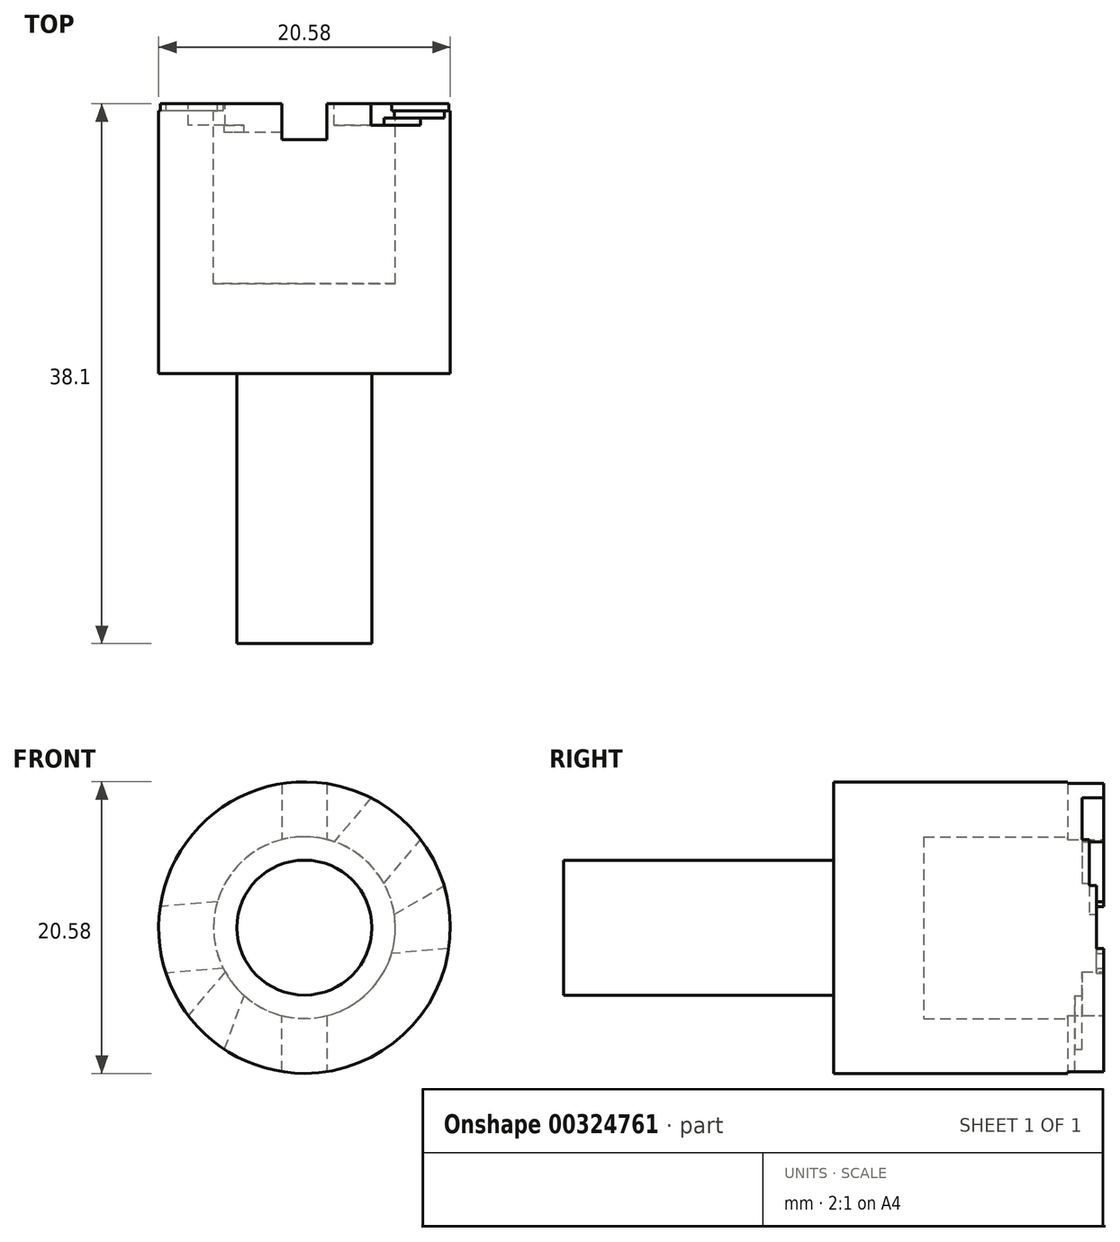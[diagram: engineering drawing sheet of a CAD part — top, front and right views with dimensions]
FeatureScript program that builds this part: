
annotation { "Feature Type Name" : "Feature", "Feature Type Description" : "" }
export const myFeature = defineFeature(function(context is Context, id is Id, definition is map)
    precondition{}
    {
        {
            var Q0;
            Q0=qCreatedBy(makeId("Front.planeOp"),FACE);
            var sketch = newSketch(context, id + "F0", { "sketchPlane" : qUnion([Q0])});
            skCircle(sketch, "E0", {"center": v(0, 0) * mm, "radius": 10.29 * mm});
            skSolve(sketch);
        }
        {
            var Q0;
            Q0=makeQuery(id+"F0.imprint","IMPRINT",FACE,{"disambiguationData":[TD([[makeQuery(id+"F0.imprint","IMPRINT",EDGE,{"derivedFrom":sQuery(id+"F0.wireOp",EDGE,"E0")}),1.0]])]});
            extrude(context, id + "F1", {"entities" : qUnion([Q0]), "depth" : 38.1 * mm, "offsetDistance" : 25.4 * mm});
        }
        {
            var Q0;
            Q0=makeQuery(id+"F1.opExtrude","CAP_FACE",FACE,{"disambiguationData":[OSD([sQuery(id+"F0.wireOp",EDGE,"E0")])],"isStart":false});
            var sketch = newSketch(context, id + "F2", { "sketchPlane" : qUnion([Q0])});
            skCircle(sketch, "E1", {"center": v(0, 0) * mm, "radius": 4.76 * mm});
            skCircle(sketch, "E2", {"center": v(0, 0) * mm, "radius": 10.29 * mm});
            skSolve(sketch);
        }
        {
            var Q0;
            Q0=makeQuery(id+"F2.imprint","IMPRINT",FACE,{"disambiguationData":[TD([[makeQuery(id+"F2.imprint","IMPRINT",EDGE,{"derivedFrom":sQuery(id+"F2.wireOp",EDGE,"E1")}),-1.0]])]});
            extrude(context, id + "F3", {"entities" : qUnion([Q0]), "operationType" : NewBodyOperationType.REMOVE, "oppositeDirection" : true, "depth" : 19.05 * mm, "offsetDistance" : 25.4 * mm});
        }
        {
            var Q0;
            Q0=makeQuery(id+"F1.opExtrude","CAP_FACE",FACE,{"disambiguationData":[OSD([sQuery(id+"F0.wireOp",EDGE,"E0")])],"isStart":true});
            var sketch = newSketch(context, id + "F4", { "sketchPlane" : qUnion([Q0])});
            skCircle(sketch, "E3", {"center": v(0, 0) * mm, "radius": 6.41 * mm});
            skSolve(sketch);
        }
        {
            var Q0;
            Q0=makeQuery(id+"F4.imprint","IMPRINT",FACE,{"disambiguationData":[TD([[makeQuery(id+"F4.imprint","IMPRINT",EDGE,{"derivedFrom":sQuery(id+"F4.wireOp",EDGE,"E3")}),1.0]])]});
            extrude(context, id + "F5", {"entities" : qUnion([Q0]), "operationType" : NewBodyOperationType.REMOVE, "oppositeDirection" : true, "depth" : 12.7 * mm, "offsetDistance" : 25.4 * mm});
        }
        {
            var Q0;
            Q0=makeQuery(id+"F1.opExtrude","CAP_FACE",FACE,{"disambiguationData":[OSD([sQuery(id+"F0.wireOp",EDGE,"E0")])],"isStart":true});
            var sketch = newSketch(context, id + "F6", { "sketchPlane" : qUnion([Q0])});
            skLineSegment(sketch, "E4.bottom", {"start": v(-1.57, 12.92) * mm, "end": v(1.6, 12.92) * mm});
            skLineSegment(sketch, "E4.top", {"start": v(-1.57, -12.85) * mm, "end": v(1.6, -12.85) * mm});
            skLineSegment(sketch, "E4.left", {"start": v(-1.57, 12.92) * mm, "end": v(-1.57, -12.85) * mm});
            skLineSegment(sketch, "E4.right", {"start": v(1.6, 12.92) * mm, "end": v(1.6, -12.85) * mm});
            skSolve(sketch);
        }
        {
            var Q0;
            {var subQ0=sQuery(id+"F6.wireOp",EDGE,"E4.left");var subQ1=makeQuery(id+"F1.opExtrude","CAP_EDGE",EDGE,{"disambiguationData":[OSD([sQuery(id+"F0.wireOp",EDGE,"E0")])],"isStart":true});var subQ2=makeQuery(id+"F6.imprint","INTERSECT",VERTEX,{"disambiguationData":[OD(0.0)],"derivedFrom":[subQ1,subQ0]});Q0=makeQuery(id+"F6.imprint","IMPRINT",FACE,{"disambiguationData":[TD([[makeQuery(id+"F6.imprint","IMPRINT",EDGE,{"disambiguationData":[TD([[subQ2,-1.0]])],"derivedFrom":subQ0}),1.0]])]});}
            var Q1;
            {var subQ0=sQuery(id+"F6.wireOp",EDGE,"E4.left");var subQ1=makeQuery(id+"F1.opExtrude","CAP_EDGE",EDGE,{"disambiguationData":[OSD([sQuery(id+"F0.wireOp",EDGE,"E0")])],"isStart":true});var subQ2=makeQuery(id+"F6.imprint","INTERSECT",VERTEX,{"disambiguationData":[OD(1.0)],"derivedFrom":[subQ1,subQ0]});Q1=makeQuery(id+"F6.imprint","IMPRINT",FACE,{"disambiguationData":[TD([[makeQuery(id+"F6.imprint","IMPRINT",EDGE,{"disambiguationData":[TD([[subQ2,1.0]])],"derivedFrom":subQ0}),1.0]])]});}
            extrude(context, id + "F7", {"entities" : qUnion([Q0, Q1]), "operationType" : NewBodyOperationType.REMOVE, "oppositeDirection" : true, "depth" : 2.54 * mm, "offsetDistance" : 25.4 * mm});
        }
        {
            var Q0;
            {var subQ0=sQuery(id+"F0.wireOp",EDGE,"E0");var subQ2=sQuery(id+"F6.wireOp",EDGE,"E4.left");var subQ3=makeQuery(id+"F1.opExtrude","CAP_EDGE",EDGE,{"disambiguationData":[OSD([subQ0])],"isStart":true});Q0=makeQuery(id+"F7.boolean.opBoolean","SPLIT",FACE,{"disambiguationData":[TD([makeQuery(id+"F7.opExtrude","SWEPT_FACE",FACE,{"disambiguationData":[OSD([subQ2]),TDD([makeQuery(id+"F6.imprint","IMPRINT",EDGE,{"disambiguationData":[TD([[makeQuery(id+"F6.imprint","INTERSECT",VERTEX,{"disambiguationData":[OD(0.0)],"derivedFrom":[subQ3,subQ2]}),-1.0]])],"derivedFrom":subQ2})])]})])],"derivedFrom":makeQuery(id+"F1.opExtrude","CAP_FACE",FACE,{"disambiguationData":[OSD([subQ0])],"isStart":true})});}
            var sketch = newSketch(context, id + "F8", { "sketchPlane" : qUnion([Q0])});
            skLineSegment(sketch, "E5", {"start": v(0, 0) * mm, "end": v(-4.44, 12.2) * mm, "construction": true});
            skLineSegment(sketch, "E6", {"start": v(-6.13, 9.93) * mm, "end": v(1.69, -11.55) * mm});
            skLineSegment(sketch, "E7.MirrorCS", {"start": v(-1.69, 11.55) * mm, "end": v(6.13, -9.93) * mm});
            skLineSegment(sketch, "E8", {"start": v(-6.13, 9.93) * mm, "end": v(-1.69, 11.55) * mm});
            skLineSegment(sketch, "E9", {"start": v(1.69, -11.55) * mm, "end": v(6.13, -9.93) * mm});
            skSolve(sketch);
        }
        {
            var Q0;
            {var subQ1=sQuery(id+"F0.wireOp",EDGE,"E0");var subQ3=sQuery(id+"F6.wireOp",EDGE,"E4.left");var subQ4=makeQuery(id+"F1.opExtrude","CAP_EDGE",EDGE,{"disambiguationData":[OSD([subQ1])],"isStart":true});var subQ7=makeQuery(id+"F6.imprint","IMPRINT",EDGE,{"disambiguationData":[TD([[makeQuery(id+"F6.imprint","INTERSECT",VERTEX,{"disambiguationData":[OD(0.0)],"derivedFrom":[subQ4,subQ3]}),-1.0]])],"derivedFrom":subQ3});var subQ14=makeQuery(id+"F7.boolean.opBoolean","COPY",EDGE,{"derivedFrom":makeQuery(id+"F7.opExtrude","CAP_EDGE",EDGE,{"disambiguationData":[OSD([subQ3]),TDD([subQ7])],"isStart":true})});Q0=makeQuery(id+"F8.imprint","IMPRINT",FACE,{"disambiguationData":[TD([[makeQuery(id+"F8.imprint","IMPRINT",EDGE,{"derivedFrom":subQ14}),-1.0]])]});}
            var Q1;
            Q1=makeQuery(id+"F8.imprint","IMPRINT",FACE,{"disambiguationData":[TD([[makeQuery(id+"F8.imprint","IMPRINT",EDGE,{"derivedFrom":sQuery(id+"F8.wireOp",EDGE,"E7.MirrorCS")}),-1.0]])]});
            var Q2;
            {var subQ1=sQuery(id+"F0.wireOp",EDGE,"E0");var subQ3=sQuery(id+"F6.wireOp",EDGE,"E4.left");var subQ4=makeQuery(id+"F1.opExtrude","CAP_EDGE",EDGE,{"disambiguationData":[OSD([subQ1])],"isStart":true});var subQ7=makeQuery(id+"F6.imprint","IMPRINT",EDGE,{"disambiguationData":[TD([[makeQuery(id+"F6.imprint","INTERSECT",VERTEX,{"disambiguationData":[OD(0.0)],"derivedFrom":[subQ4,subQ3]}),-1.0]])],"derivedFrom":subQ3});var subQ12=sQuery(id+"F8.wireOp",EDGE,"E7.MirrorCS");var subQ15=makeQuery(id+"F7.boolean.opBoolean","COPY",EDGE,{"derivedFrom":makeQuery(id+"F7.opExtrude","CAP_EDGE",EDGE,{"disambiguationData":[OSD([subQ3]),TDD([subQ7])],"isStart":true})});var subQ17=makeQuery(id+"F8.imprint","INTERSECT",VERTEX,{"derivedFrom":[subQ15,subQ12]});Q2=makeQuery(id+"F8.imprint","IMPRINT",FACE,{"disambiguationData":[TD([[makeQuery(id+"F8.imprint","IMPRINT",EDGE,{"disambiguationData":[TD([[subQ17,1.0]])],"derivedFrom":subQ12}),-1.0]])]});}
            var Q3;
            {var subQ11=sQuery(id+"F8.wireOp",EDGE,"E9");Q3=makeQuery(id+"F8.imprint","IMPRINT",FACE,{"disambiguationData":[TD([[makeQuery(id+"F8.imprint","IMPRINT",EDGE,{"derivedFrom":subQ11}),1.0]])]});}
            extrude(context, id + "F9", {"entities" : qUnion([Q0, Q1, Q2, Q3]), "operationType" : NewBodyOperationType.REMOVE, "oppositeDirection" : true, "depth" : 2.03 * mm, "offsetDistance" : 25.4 * mm});
        }
        {
            var Q0;
            {var subQ0=sQuery(id+"F0.wireOp",EDGE,"E0");var subQ2=sQuery(id+"F6.wireOp",EDGE,"E4.left");var subQ3=makeQuery(id+"F1.opExtrude","CAP_EDGE",EDGE,{"disambiguationData":[OSD([subQ0])],"isStart":true});Q0=makeQuery(id+"F7.boolean.opBoolean","SPLIT",FACE,{"disambiguationData":[TD([makeQuery(id+"F7.opExtrude","SWEPT_FACE",FACE,{"disambiguationData":[OSD([subQ2]),TDD([makeQuery(id+"F6.imprint","IMPRINT",EDGE,{"disambiguationData":[TD([[makeQuery(id+"F6.imprint","INTERSECT",VERTEX,{"disambiguationData":[OD(0.0)],"derivedFrom":[subQ3,subQ2]}),-1.0]])],"derivedFrom":subQ2})])]})])],"derivedFrom":makeQuery(id+"F1.opExtrude","CAP_FACE",FACE,{"disambiguationData":[OSD([subQ0])],"isStart":true})});}
            var sketch = newSketch(context, id + "F10", { "sketchPlane" : qUnion([Q0])});
            skLineSegment(sketch, "E10", {"start": v(0, 0) * mm, "end": v(-6.57, 7.83) * mm, "construction": true});
            skLineSegment(sketch, "E11", {"start": v(-9.1, 7.29) * mm, "end": v(5.6, -10.23) * mm});
            skLineSegment(sketch, "E12.MirrorCS", {"start": v(-5.6, 10.23) * mm, "end": v(9.1, -7.29) * mm});
            skLineSegment(sketch, "E13", {"start": v(-5.6, 10.23) * mm, "end": v(-9.1, 7.29) * mm});
            skLineSegment(sketch, "E14", {"start": v(5.6, -10.23) * mm, "end": v(9.1, -7.29) * mm});
            skSolve(sketch);
        }
        {
            var Q0;
            {var subQ13=makeQuery(id+"F9.boolean.opBoolean","COPY",EDGE,{"derivedFrom":makeQuery(id+"F9.opExtrude","CAP_EDGE",EDGE,{"disambiguationData":[OSD([sQuery(id+"F8.wireOp",EDGE,"E6")])],"isStart":true})});Q0=makeQuery(id+"F10.imprint","IMPRINT",FACE,{"disambiguationData":[TD([[makeQuery(id+"F10.imprint","IMPRINT",EDGE,{"derivedFrom":subQ13}),-1.0]])]});}
            var Q1;
            Q1=makeQuery(id+"F10.imprint","IMPRINT",FACE,{"disambiguationData":[TD([[makeQuery(id+"F10.imprint","IMPRINT",EDGE,{"derivedFrom":sQuery(id+"F10.wireOp",EDGE,"E12.MirrorCS")}),-1.0]])]});
            var Q2;
            {var subQ2=sQuery(id+"F8.wireOp",EDGE,"E6");var subQ4=sQuery(id+"F4.wireOp",EDGE,"E3");var subQ5=makeQuery(id+"F5.boolean.opBoolean","COPY",FACE,{"derivedFrom":makeQuery(id+"F5.opExtrude","SWEPT_FACE",FACE,{"disambiguationData":[OSD([subQ4])]})});var subQ6=makeQuery(id+"F9.boolean.opBoolean","COPY",EDGE,{"disambiguationData":[TD([subQ5])],"derivedFrom":makeQuery(id+"F9.opExtrude","CAP_EDGE",EDGE,{"disambiguationData":[OSD([subQ2])],"isStart":true})});var subQ16=sQuery(id+"F10.wireOp",EDGE,"E12.MirrorCS");var subQ19=makeQuery(id+"F10.imprint","INTERSECT",VERTEX,{"derivedFrom":[subQ6,subQ16]});Q2=makeQuery(id+"F10.imprint","IMPRINT",FACE,{"disambiguationData":[TD([[makeQuery(id+"F10.imprint","IMPRINT",EDGE,{"disambiguationData":[TD([[subQ19,1.0]])],"derivedFrom":subQ16}),-1.0]])]});}
            var Q3;
            {var subQ13=sQuery(id+"F10.wireOp",EDGE,"E14");Q3=makeQuery(id+"F10.imprint","IMPRINT",FACE,{"disambiguationData":[TD([[makeQuery(id+"F10.imprint","IMPRINT",EDGE,{"derivedFrom":subQ13}),1.0]])]});}
            extrude(context, id + "F11", {"entities" : qUnion([Q0, Q1, Q2, Q3]), "operationType" : NewBodyOperationType.REMOVE, "oppositeDirection" : true, "depth" : 1.52 * mm, "offsetDistance" : 25.4 * mm});
        }
        {
            var Q0;
            {var subQ0=sQuery(id+"F0.wireOp",EDGE,"E0");var subQ2=sQuery(id+"F6.wireOp",EDGE,"E4.right");var subQ3=makeQuery(id+"F1.opExtrude","CAP_EDGE",EDGE,{"disambiguationData":[OSD([subQ0])],"isStart":true});Q0=makeQuery(id+"F7.boolean.opBoolean","SPLIT",FACE,{"disambiguationData":[TD([makeQuery(id+"F7.opExtrude","SWEPT_FACE",FACE,{"disambiguationData":[OSD([subQ2]),TDD([makeQuery(id+"F6.imprint","IMPRINT",EDGE,{"disambiguationData":[TD([[makeQuery(id+"F6.imprint","INTERSECT",VERTEX,{"disambiguationData":[OD(0.0)],"derivedFrom":[subQ3,subQ2]}),-1.0]])],"derivedFrom":subQ2})])]})])],"derivedFrom":makeQuery(id+"F1.opExtrude","CAP_FACE",FACE,{"disambiguationData":[OSD([subQ0])],"isStart":true})});}
            var sketch = newSketch(context, id + "F12", { "sketchPlane" : qUnion([Q0])});
            skLineSegment(sketch, "E15", {"start": v(0, 0) * mm, "end": v(-19.87, 11.47) * mm, "construction": true});
            skLineSegment(sketch, "E16", {"start": v(-17.08, 7.13) * mm, "end": v(15.38, -11.6) * mm});
            skLineSegment(sketch, "E17.MirrorCS", {"start": v(-14.71, 11.22) * mm, "end": v(17.74, -7.52) * mm});
            skLineSegment(sketch, "E18", {"start": v(-17.08, 7.13) * mm, "end": v(-14.71, 11.22) * mm});
            skLineSegment(sketch, "E19", {"start": v(17.74, -7.52) * mm, "end": v(15.38, -11.6) * mm});
            skSolve(sketch);
        }
        {
            var Q0;
            Q0=makeQuery(id+"F12.imprint","IMPRINT",FACE,{"disambiguationData":[TD([[makeQuery(id+"F12.imprint","IMPRINT",EDGE,{"derivedFrom":sQuery(id+"F12.wireOp",EDGE,"E16")}),1.0]])]});
            var Q1;
            {var subQ13=makeQuery(id+"F11.boolean.opBoolean","COPY",EDGE,{"derivedFrom":makeQuery(id+"F11.opExtrude","CAP_EDGE",EDGE,{"disambiguationData":[OSD([sQuery(id+"F10.wireOp",EDGE,"E12.MirrorCS")])],"isStart":true})});Q1=makeQuery(id+"F12.imprint","IMPRINT",FACE,{"disambiguationData":[TD([[makeQuery(id+"F12.imprint","IMPRINT",EDGE,{"derivedFrom":subQ13}),1.0]])]});}
            var Q2;
            {var subQ14=sQuery(id+"F12.wireOp",EDGE,"E18");Q2=makeQuery(id+"F12.imprint","IMPRINT",FACE,{"disambiguationData":[TD([[makeQuery(id+"F12.imprint","IMPRINT",EDGE,{"derivedFrom":subQ14}),-1.0]])]});}
            var Q3;
            {var subQ10=sQuery(id+"F10.wireOp",EDGE,"E12.MirrorCS");var subQ13=makeQuery(id+"F10.imprint","IMPRINT",EDGE,{"disambiguationData":[TD([[makeQuery(id+"F10.imprint","INTERSECT",VERTEX,{"derivedFrom":[subQ10,sQuery(id+"F10.wireOp",EDGE,"E14")]}),1.0]])],"derivedFrom":subQ10});var subQ14=makeQuery(id+"F11.boolean.opBoolean","COPY",EDGE,{"derivedFrom":makeQuery(id+"F11.opExtrude","CAP_EDGE",EDGE,{"disambiguationData":[OSD([subQ10]),TDD([subQ13])],"isStart":true})});var subQ23=sQuery(id+"F12.wireOp",EDGE,"E16");var subQ24=makeQuery(id+"F12.imprint","INTERSECT",VERTEX,{"derivedFrom":[subQ14,subQ23]});Q3=makeQuery(id+"F12.imprint","IMPRINT",FACE,{"disambiguationData":[TD([[makeQuery(id+"F12.imprint","IMPRINT",EDGE,{"disambiguationData":[TD([[subQ24,1.0]])],"derivedFrom":subQ14}),1.0]])]});}
            extrude(context, id + "F13", {"entities" : qUnion([Q0, Q1, Q2, Q3]), "operationType" : NewBodyOperationType.REMOVE, "oppositeDirection" : true, "depth" : 1.02 * mm, "offsetDistance" : 25.4 * mm});
        }
        {
            var Q0;
            {var subQ0=sQuery(id+"F0.wireOp",EDGE,"E0");var subQ2=sQuery(id+"F6.wireOp",EDGE,"E4.left");var subQ3=makeQuery(id+"F1.opExtrude","CAP_EDGE",EDGE,{"disambiguationData":[OSD([subQ0])],"isStart":true});Q0=makeQuery(id+"F7.boolean.opBoolean","SPLIT",FACE,{"disambiguationData":[TD([makeQuery(id+"F7.opExtrude","SWEPT_FACE",FACE,{"disambiguationData":[OSD([subQ2]),TDD([makeQuery(id+"F6.imprint","IMPRINT",EDGE,{"disambiguationData":[TD([[makeQuery(id+"F6.imprint","INTERSECT",VERTEX,{"disambiguationData":[OD(0.0)],"derivedFrom":[subQ3,subQ2]}),-1.0]])],"derivedFrom":subQ2})])]})])],"derivedFrom":makeQuery(id+"F1.opExtrude","CAP_FACE",FACE,{"disambiguationData":[OSD([subQ0])],"isStart":true})});}
            var sketch = newSketch(context, id + "F14", { "sketchPlane" : qUnion([Q0])});
            skLineSegment(sketch, "E20", {"start": v(0, 0) * mm, "end": v(-33.9, 2.97) * mm, "construction": true});
            skLineSegment(sketch, "E21", {"start": v(-26.22, -0.08) * mm, "end": v(22.55, -4.34) * mm});
            skLineSegment(sketch, "E22.MirrorCS", {"start": v(-25.8, 4.63) * mm, "end": v(22.96, 0.36) * mm});
            skLineSegment(sketch, "E23", {"start": v(-26.22, -0.08) * mm, "end": v(-25.8, 4.63) * mm});
            skLineSegment(sketch, "E24", {"start": v(22.96, 0.36) * mm, "end": v(22.55, -4.34) * mm});
            skSolve(sketch);
        }
        {
            var Q0;
            {var subQ15=sQuery(id+"F14.wireOp",EDGE,"E24");Q0=makeQuery(id+"F14.imprint","IMPRINT",FACE,{"disambiguationData":[TD([[makeQuery(id+"F14.imprint","IMPRINT",EDGE,{"derivedFrom":subQ15}),-1.0]])]});}
            var Q1;
            {var subQ10=sQuery(id+"F12.wireOp",EDGE,"E16");var subQ14=makeQuery(id+"F12.imprint","IMPRINT",EDGE,{"disambiguationData":[TD([[makeQuery(id+"F12.imprint","INTERSECT",VERTEX,{"derivedFrom":[subQ10,sQuery(id+"F12.wireOp",EDGE,"E18")]}),-1.0]])],"derivedFrom":subQ10});var subQ15=makeQuery(id+"F13.boolean.opBoolean","COPY",EDGE,{"derivedFrom":makeQuery(id+"F13.opExtrude","CAP_EDGE",EDGE,{"disambiguationData":[OSD([subQ10]),TDD([subQ14])],"isStart":true})});var subQ19=sQuery(id+"F14.wireOp",EDGE,"E22.MirrorCS");var subQ22=makeQuery(id+"F14.imprint","INTERSECT",VERTEX,{"derivedFrom":[subQ15,subQ19]});Q1=makeQuery(id+"F14.imprint","IMPRINT",FACE,{"disambiguationData":[TD([[makeQuery(id+"F14.imprint","IMPRINT",EDGE,{"disambiguationData":[TD([[subQ22,-1.0]])],"derivedFrom":subQ15}),-1.0]])]});}
            extrude(context, id + "F15", {"entities" : qUnion([Q0, Q1]), "operationType" : NewBodyOperationType.REMOVE, "oppositeDirection" : true, "depth" : 0.5 * mm, "offsetDistance" : 25.4 * mm});
        }
    });
